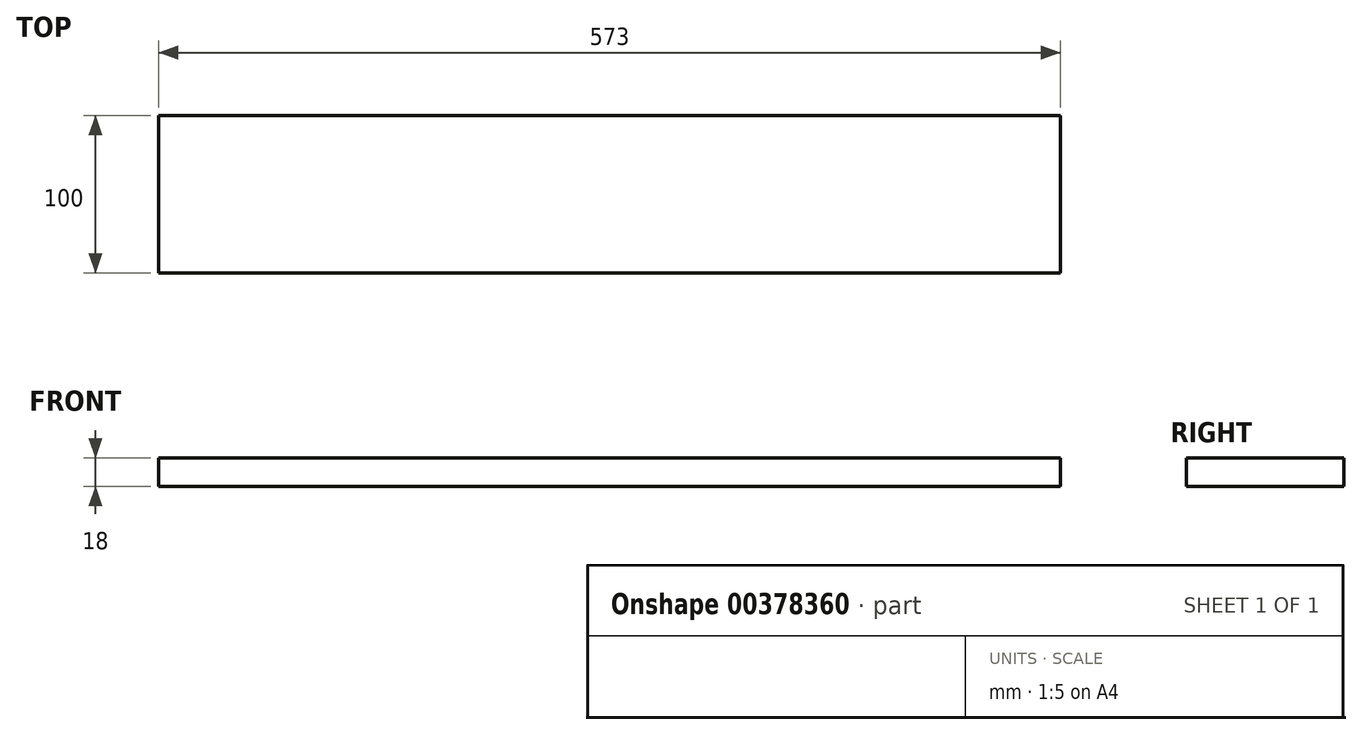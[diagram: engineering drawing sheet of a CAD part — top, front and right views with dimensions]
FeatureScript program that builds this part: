
annotation { "Feature Type Name" : "Feature", "Feature Type Description" : "" }
export const myFeature = defineFeature(function(context is Context, id is Id, definition is map)
    precondition{}
    {
        {
            var Q0;
            Q0=qCreatedBy(makeId("Right.planeOp"),FACE);
            var sketch = newSketch(context, id + "F0", { "sketchPlane" : qUnion([Q0])});
            skLineSegment(sketch, "E0.bottom", {"start": v(50, 9) * mm, "end": v(-50, 9) * mm});
            skLineSegment(sketch, "E0.top", {"start": v(50, -9) * mm, "end": v(-50, -9) * mm});
            skLineSegment(sketch, "E0.left", {"start": v(50, 9) * mm, "end": v(50, -9) * mm});
            skLineSegment(sketch, "E0.right", {"start": v(-50, 9) * mm, "end": v(-50, -9) * mm});
            skPoint(sketch, "E0.middle", {"position": v(0, 0) * mm});
            skSolve(sketch);
        }
        {
            var Q0;
            Q0 = qSketchRegion(id + "F0", true);
            extrude(context, id + "F1", {"entities" : qUnion([Q0]), "depth" : 573 * mm});
        }
    });
